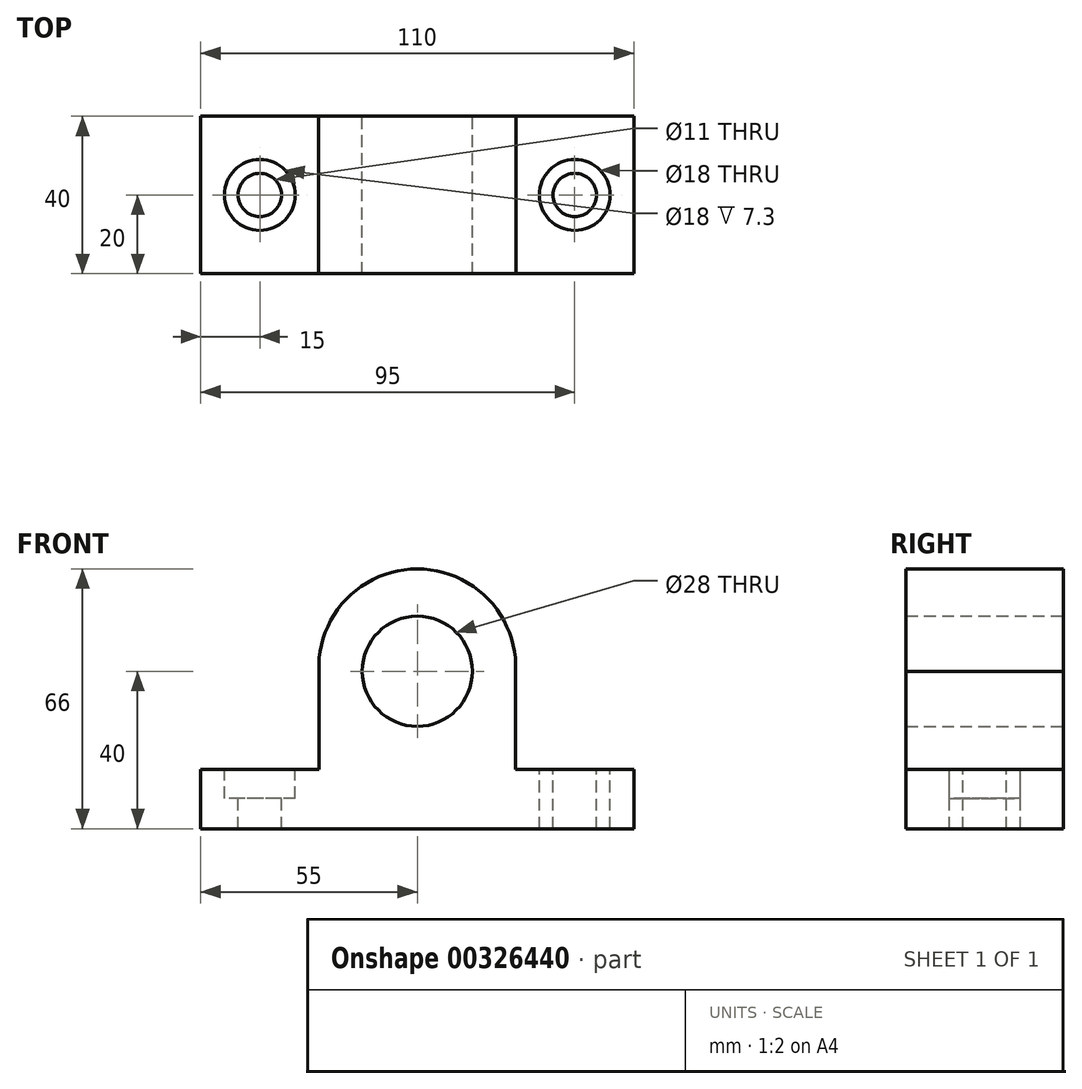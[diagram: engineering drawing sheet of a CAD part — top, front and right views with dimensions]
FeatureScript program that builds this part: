
annotation { "Feature Type Name" : "Feature", "Feature Type Description" : "" }
export const myFeature = defineFeature(function(context is Context, id is Id, definition is map)
    precondition{}
    {
        {
            var Q0;
            Q0=qCreatedBy(makeId("Front.planeOp"),FACE);
            var sketch = newSketch(context, id + "F0", { "sketchPlane" : qUnion([Q0])});
            skLineSegment(sketch, "E0", {"start": v(0, 66.72) * mm, "end": v(0, -60.4) * mm, "construction": true});
            skLineSegment(sketch, "E1", {"start": v(0, 0) * mm, "end": v(-55, 0) * mm});
            skLineSegment(sketch, "E2", {"start": v(-55, 0) * mm, "end": v(-55, 15) * mm});
            skLineSegment(sketch, "E3", {"start": v(-55, 15) * mm, "end": v(-25, 15) * mm});
            skLineSegment(sketch, "E4", {"start": v(-25, 15) * mm, "end": v(-25, 40) * mm});
            skLineSegment(sketch, "E5.MirrorCS", {"start": v(25, 15) * mm, "end": v(25, 40) * mm});
            skLineSegment(sketch, "E6.MirrorCS", {"start": v(55, 15) * mm, "end": v(25, 15) * mm});
            skLineSegment(sketch, "E7.MirrorCS", {"start": v(55, 0) * mm, "end": v(55, 15) * mm});
            skLineSegment(sketch, "E8.MirrorCS", {"start": v(0, 0) * mm, "end": v(55, 0) * mm});
            skCircle(sketch, "E9", {"center": v(0, 40) * mm, "radius": 14 * mm});
            skArc(sketch, "E10.trimOffspring", {"start": v(25, 40) * mm, "mid": v(0, 66) * mm, "end": v(-25, 40) * mm});
            skSolve(sketch);
        }
        {
            var Q0;
            Q0 = qSketchRegion(id + "F0", true);
            extrude(context, id + "F1", {"entities" : qUnion([Q0]), "depth" : 40 * mm});
        }
        {
            var Q0;
            Q0=makeQuery(id+"F1.opExtrude","SWEPT_FACE",FACE,{"disambiguationData":[OSD([sQuery(id+"F0.wireOp",EDGE,"E3")])]});
            var sketch = newSketch(context, id + "F2", { "sketchPlane" : qUnion([Q0])});
            skCircle(sketch, "E11", {"center": v(-40, -20) * mm, "radius": 9 * mm});
            skCircle(sketch, "E12", {"center": v(-40, -20) * mm, "radius": 5.5 * mm});
            skLineSegment(sketch, "E13", {"start": v(0, 19.53) * mm, "end": v(0, -44.43) * mm, "construction": true});
            skCircle(sketch, "E14.MirrorC", {"center": v(40, -20) * mm, "radius": 9 * mm});
            skCircle(sketch, "E15.MirrorC", {"center": v(40, -20) * mm, "radius": 5.5 * mm});
            skSolve(sketch);
        }
        {
            var Q0;
            Q0=makeQuery(id+"F2.imprint","IMPRINT",FACE,{"disambiguationData":[TD([[makeQuery(id+"F2.imprint","IMPRINT",EDGE,{"derivedFrom":sQuery(id+"F2.wireOp",EDGE,"E15.MirrorC")}),-1.0]])]});
            var Q1;
            Q1=makeQuery(id+"F2.imprint","IMPRINT",FACE,{"disambiguationData":[TD([[makeQuery(id+"F2.imprint","IMPRINT",EDGE,{"derivedFrom":sQuery(id+"F2.wireOp",EDGE,"E12")}),1.0]])]});
            extrude(context, id + "F3", {"entities" : qUnion([Q0, Q1]), "operationType" : NewBodyOperationType.REMOVE, "oppositeDirection" : true, "depth" : 15 * mm});
        }
        {
            var Q0;
            Q0=makeQuery(id+"F2.imprint","IMPRINT",FACE,{"disambiguationData":[TD([[makeQuery(id+"F2.imprint","IMPRINT",EDGE,{"derivedFrom":sQuery(id+"F2.wireOp",EDGE,"E14.MirrorC")}),-1.0]])]});
            var Q1;
            Q1=makeQuery(id+"F2.imprint","IMPRINT",FACE,{"disambiguationData":[TD([[makeQuery(id+"F2.imprint","IMPRINT",EDGE,{"derivedFrom":sQuery(id+"F2.wireOp",EDGE,"E11")}),1.0]])]});
            extrude(context, id + "F4", {"entities" : qUnion([Q0, Q1]), "operationType" : NewBodyOperationType.REMOVE, "oppositeDirection" : true, "depth" : 7.3 * mm});
        }
    });
